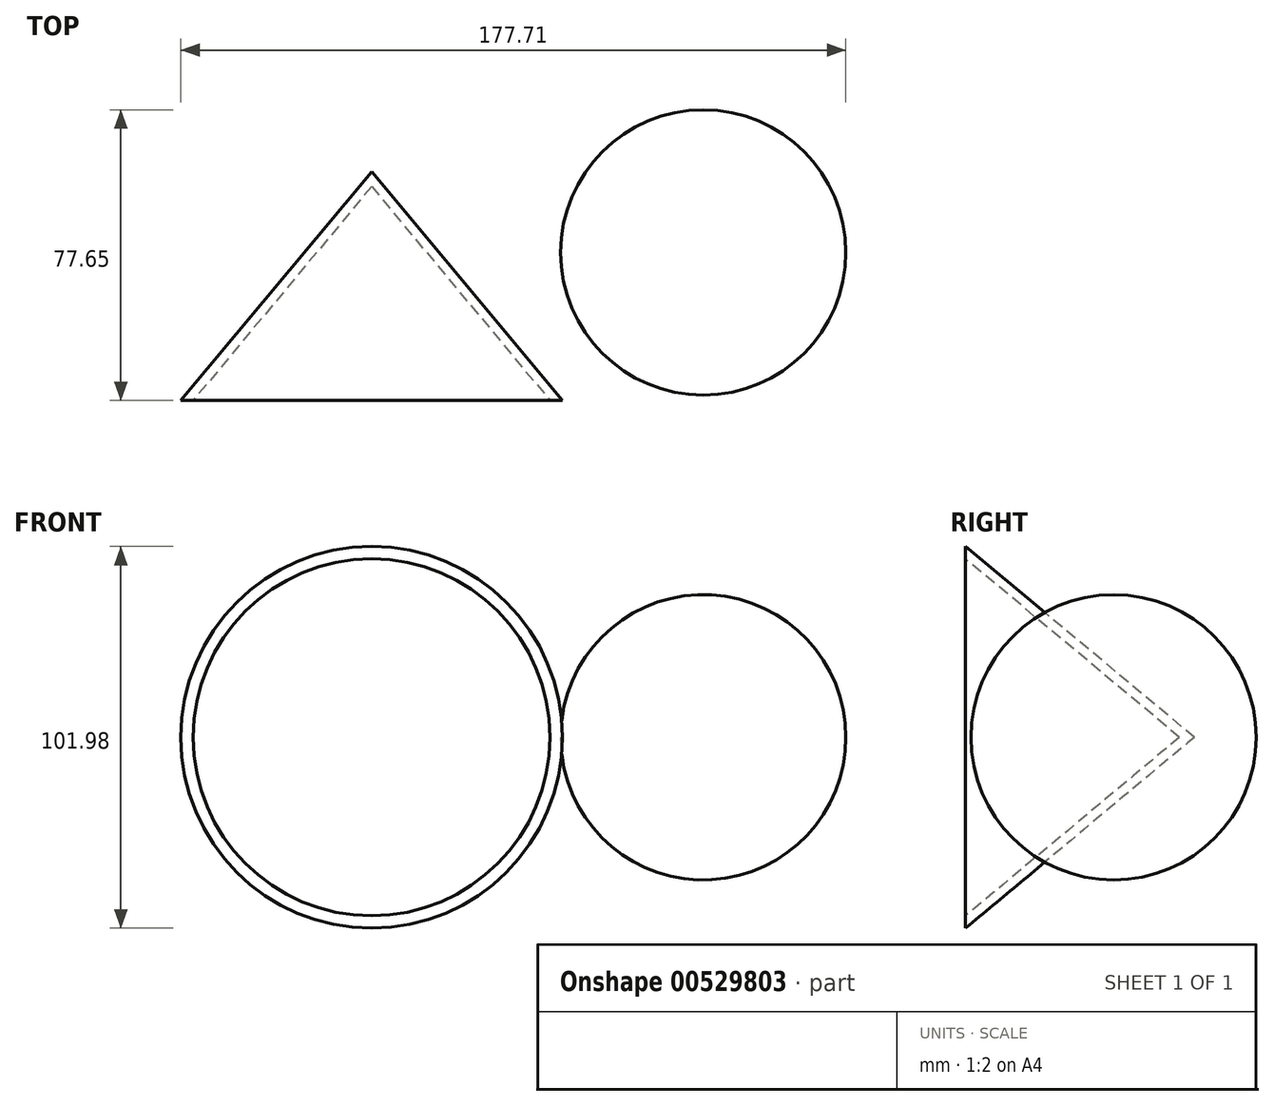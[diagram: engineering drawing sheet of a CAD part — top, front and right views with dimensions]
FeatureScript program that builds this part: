
annotation { "Feature Type Name" : "Feature", "Feature Type Description" : "" }
export const myFeature = defineFeature(function(context is Context, id is Id, definition is map)
    precondition{}
    {
        {
            var Q0;
            Q0=qCreatedBy(makeId("Top.planeOp"),FACE);
            var sketch = newSketch(context, id + "F0", { "sketchPlane" : qUnion([Q0])});
            skLineSegment(sketch, "E0", {"start": v(-50.99, 48.37) * mm, "end": v(-50.99, -12.75) * mm});
            skLineSegment(sketch, "E1", {"start": v(-50.99, -12.75) * mm, "end": v(0, -12.75) * mm});
            skLineSegment(sketch, "E2", {"start": v(0, -12.75) * mm, "end": v(-50.99, 48.37) * mm});
            skSolve(sketch);
        }
        {
            var Q0;
            Q0=makeQuery(id+"F0.imprint","IMPRINT",FACE,{"disambiguationData":[TD([[makeQuery(id+"F0.imprint","IMPRINT",EDGE,{"derivedFrom":sQuery(id+"F0.wireOp",EDGE,"E0")}),1.0]])]});
            var Q1;
            Q1=sQuery(id+"F0.wireOp",EDGE,"E0");
            revolve(context, id + "F1", {"entities" : qUnion([Q0]), "axis" : qUnion([Q1]), "revolveType" : RevolveType.FULL});
        }
        {
            var Q0;
            Q0=makeQuery(id+"F1.opRevolve","SWEPT_FACE",FACE,{"disambiguationData":[OSD([sQuery(id+"F0.wireOp",EDGE,"E1")])]});
            shell(context, id + "F2", {"entities" : qUnion([Q0]), "thickness" : 2.54 * mm});
        }
        {
            var Q0;
            Q0=qCreatedBy(makeId("Top.planeOp"),FACE);
            var sketch = newSketch(context, id + "F3", { "sketchPlane" : qUnion([Q0])});
            skLineSegment(sketch, "E3", {"start": v(-0.46, 26.8) * mm, "end": v(75.74, 26.8) * mm});
            skArc(sketch, "E4", {"start": v(75.74, 26.8) * mm, "mid": v(37.64, 64.9) * mm, "end": v(-0.46, 26.8) * mm});
            skSolve(sketch);
        }
        {
            var Q0;
            Q0=makeQuery(id+"F3.imprint","IMPRINT",FACE,{"disambiguationData":[TD([[makeQuery(id+"F3.imprint","IMPRINT",EDGE,{"derivedFrom":sQuery(id+"F3.wireOp",EDGE,"E3")}),1.0]])]});
            var Q1;
            Q1=sQuery(id+"F3.wireOp",EDGE,"E3");
            revolve(context, id + "F4", {"entities" : qUnion([Q0]), "axis" : qUnion([Q1]), "revolveType" : RevolveType.FULL});
        }
    });
